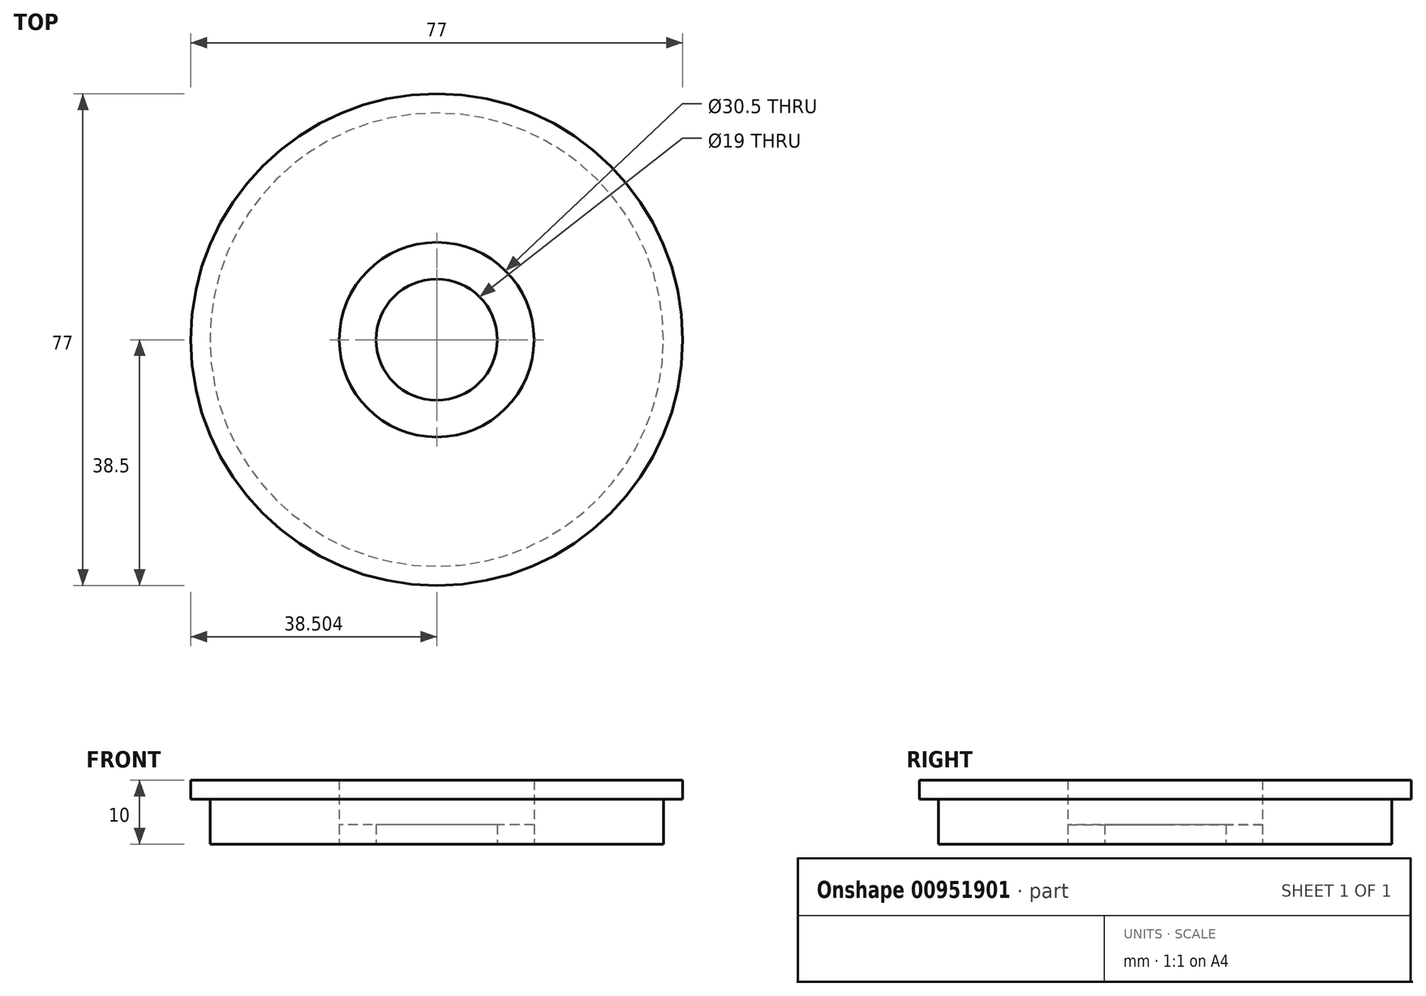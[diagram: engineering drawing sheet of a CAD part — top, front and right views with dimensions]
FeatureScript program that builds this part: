
annotation { "Feature Type Name" : "Feature", "Feature Type Description" : "" }
export const myFeature = defineFeature(function(context is Context, id is Id, definition is map)
    precondition{}
    {
        {
            var Q0;
            Q0=qCreatedBy(makeId("Top.planeOp"),FACE);
            var sketch = newSketch(context, id + "F0", { "sketchPlane" : qUnion([Q0])});
            skCircle(sketch, "E0", {"center": v(-39.15, 0) * mm, "radius": 15.25 * mm});
            skCircle(sketch, "E1", {"center": v(-39.15, 0) * mm, "radius": 35.5 * mm});
            skCircle(sketch, "E2", {"center": v(-39.15, 0) * mm, "radius": 9.5 * mm});
            skSolve(sketch);
        }
        {
            var Q0;
            Q0=makeQuery(id+"F0.imprint","IMPRINT",FACE,{"disambiguationData":[TD([[makeQuery(id+"F0.imprint","IMPRINT",EDGE,{"derivedFrom":sQuery(id+"F0.wireOp",EDGE,"E0")}),1.0]])]});
            var Q1;
            Q1=makeQuery(id+"F0.imprint","IMPRINT",FACE,{"disambiguationData":[TD([[makeQuery(id+"F0.imprint","IMPRINT",EDGE,{"derivedFrom":sQuery(id+"F0.wireOp",EDGE,"gZvZpgXt-Y5T6-j4Jx-lpFE-VRuZzmW9fOwK")}),-1.0]])]});
            extrude(context, id + "F1", {"entities" : qUnion([Q0, Q1]), "depth" : 3 * mm, "offsetDistance" : 25 * mm});
        }
        {
            var Q0;
            Q0=makeQuery(id+"F0.imprint","IMPRINT",FACE,{"disambiguationData":[TD([[makeQuery(id+"F0.imprint","IMPRINT",EDGE,{"derivedFrom":sQuery(id+"F0.wireOp",EDGE,"E0")}),-1.0]])]});
            var Q1;
            Q1=makeQuery(id+"F0.imprint","IMPRINT",FACE,{"disambiguationData":[TD([[makeQuery(id+"F0.imprint","IMPRINT",EDGE,{"derivedFrom":sQuery(id+"F0.wireOp",EDGE,"gZvZpgXt-Y5T6-j4Jx-lpFE-VRuZzmW9fOwK")}),1.0]])]});
            extrude(context, id + "F2", {"entities" : qUnion([Q0, Q1]), "depth" : 10 * mm, "offsetDistance" : 25 * mm});
        }
        {
            var Q0;
            Q0=makeQuery(id+"F2.opExtrude","CAP_FACE",FACE,{"disambiguationData":[OSD([sQuery(id+"F0.wireOp",EDGE,"E0"),sQuery(id+"F0.wireOp",EDGE,"E1")])],"isStart":false});
            var sketch = newSketch(context, id + "F3", { "sketchPlane" : qUnion([Q0])});
            skCircle(sketch, "E3", {"center": v(-39.15, 0) * mm, "radius": 38.5 * mm});
            skSolve(sketch);
        }
        {
            var Q0;
            Q0=makeQuery(id+"F3.imprint","IMPRINT",FACE,{"disambiguationData":[TD([[makeQuery(id+"F3.imprint","IMPRINT",EDGE,{"derivedFrom":sQuery(id+"F3.wireOp",EDGE,"E3")}),1.0]])]});
            extrude(context, id + "F4", {"entities" : qUnion([Q0]), "operationType" : NewBodyOperationType.ADD, "oppositeDirection" : true, "depth" : 3 * mm, "offsetDistance" : 25 * mm});
        }
    });
